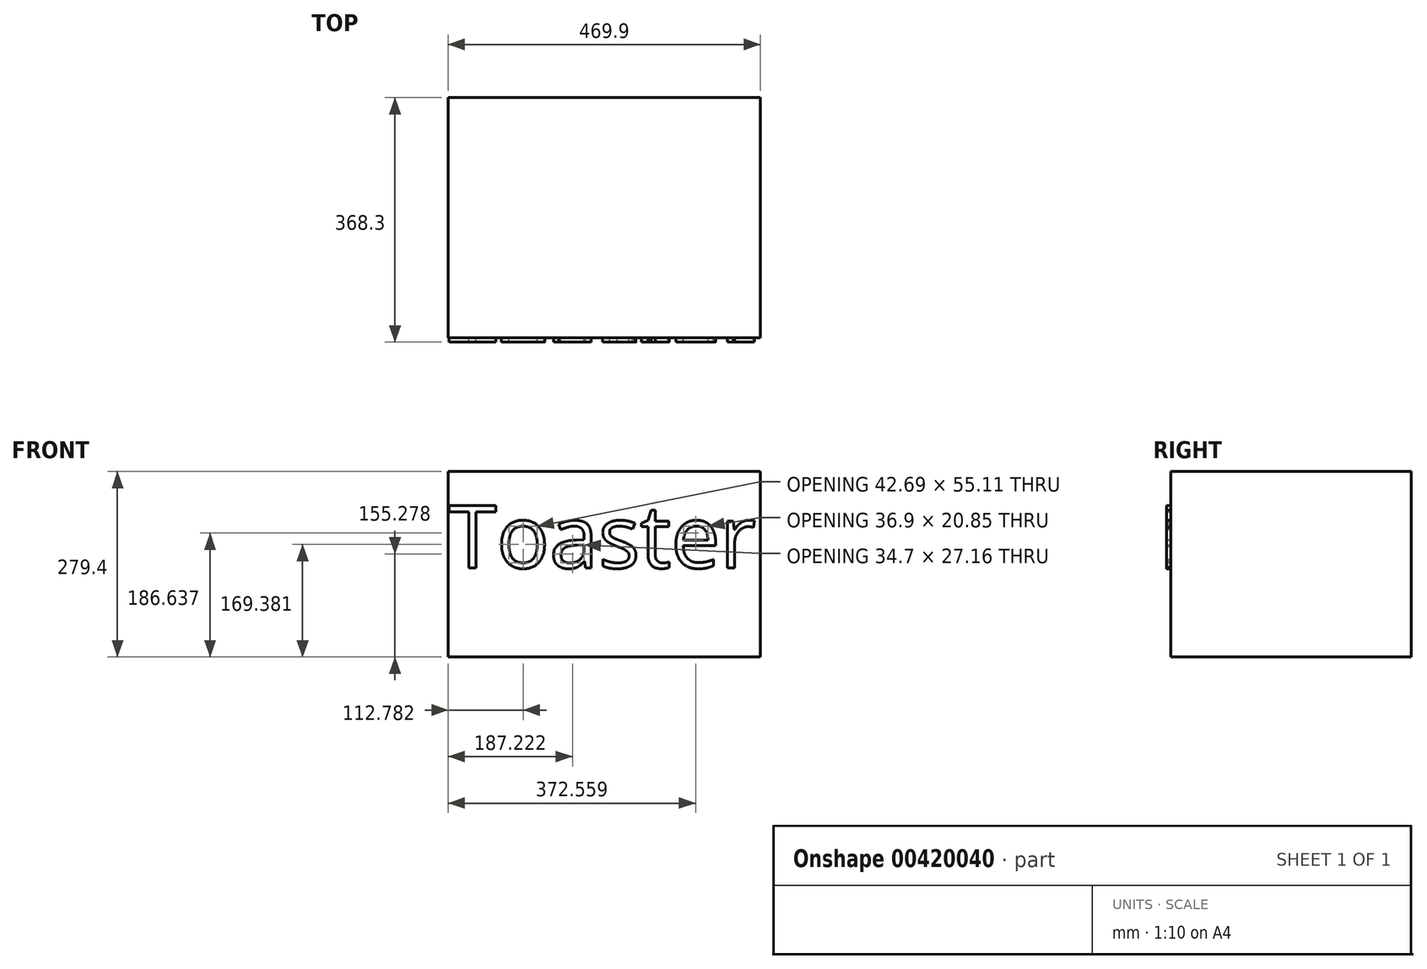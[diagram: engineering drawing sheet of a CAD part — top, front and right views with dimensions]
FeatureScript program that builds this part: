
annotation { "Feature Type Name" : "Feature", "Feature Type Description" : "" }
export const myFeature = defineFeature(function(context is Context, id is Id, definition is map)
    precondition{}
    {
        {
            var Q0;
            Q0=qCreatedBy(makeId("Front.planeOp"),FACE);
            var sketch = newSketch(context, id + "F0", { "sketchPlane" : qUnion([Q0])});
            skLineSegment(sketch, "E0.bottom", {"start": v(0, 0) * mm, "end": v(469.9, 0) * mm});
            skLineSegment(sketch, "E0.top", {"start": v(0, 279.4) * mm, "end": v(469.9, 279.4) * mm});
            skLineSegment(sketch, "E0.left", {"start": v(0, 0) * mm, "end": v(0, 279.4) * mm});
            skLineSegment(sketch, "E0.right", {"start": v(469.9, 0) * mm, "end": v(469.9, 279.4) * mm});
            skSolve(sketch);
        }
        {
            var Q0;
            Q0=makeQuery(id+"F0.imprint","IMPRINT",FACE,{"disambiguationData":[TD([[makeQuery(id+"F0.imprint","IMPRINT",EDGE,{"derivedFrom":sQuery(id+"F0.wireOp",EDGE,"E0.bottom")}),1.0]])]});
            extrude(context, id + "F1", {"entities" : qUnion([Q0]), "depth" : 361.95 * mm});
        }
        {
            var Q0;
            Q0=makeQuery(id+"F1.opExtrude","CAP_FACE",FACE,{"disambiguationData":[OSD([sQuery(id+"F0.wireOp",EDGE,"E0.bottom"),sQuery(id+"F0.wireOp",EDGE,"E0.top"),sQuery(id+"F0.wireOp",EDGE,"E0.left"),sQuery(id+"F0.wireOp",EDGE,"E0.right")])],"isStart":false});
            var sketch = newSketch(context, id + "F2", { "sketchPlane" : qUnion([Q0])});
            skText(sketch, "E1", { "text": "Toaster", "fontName": "OpenSans-Regular.ttf"});
            const initialGuessF2  = {"E1": [0, 0.13416, 1, 0, 0.09494]};
            skSetInitialGuess(sketch, initialGuessF2);
            skSolve(sketch);
        }
        {
            var Q0;
            Q0 = qSketchRegion(id + "F2", true);
            extrude(context, id + "F3", {"entities" : qUnion([Q0]), "depth" : 6.35 * mm});
        }
    });
